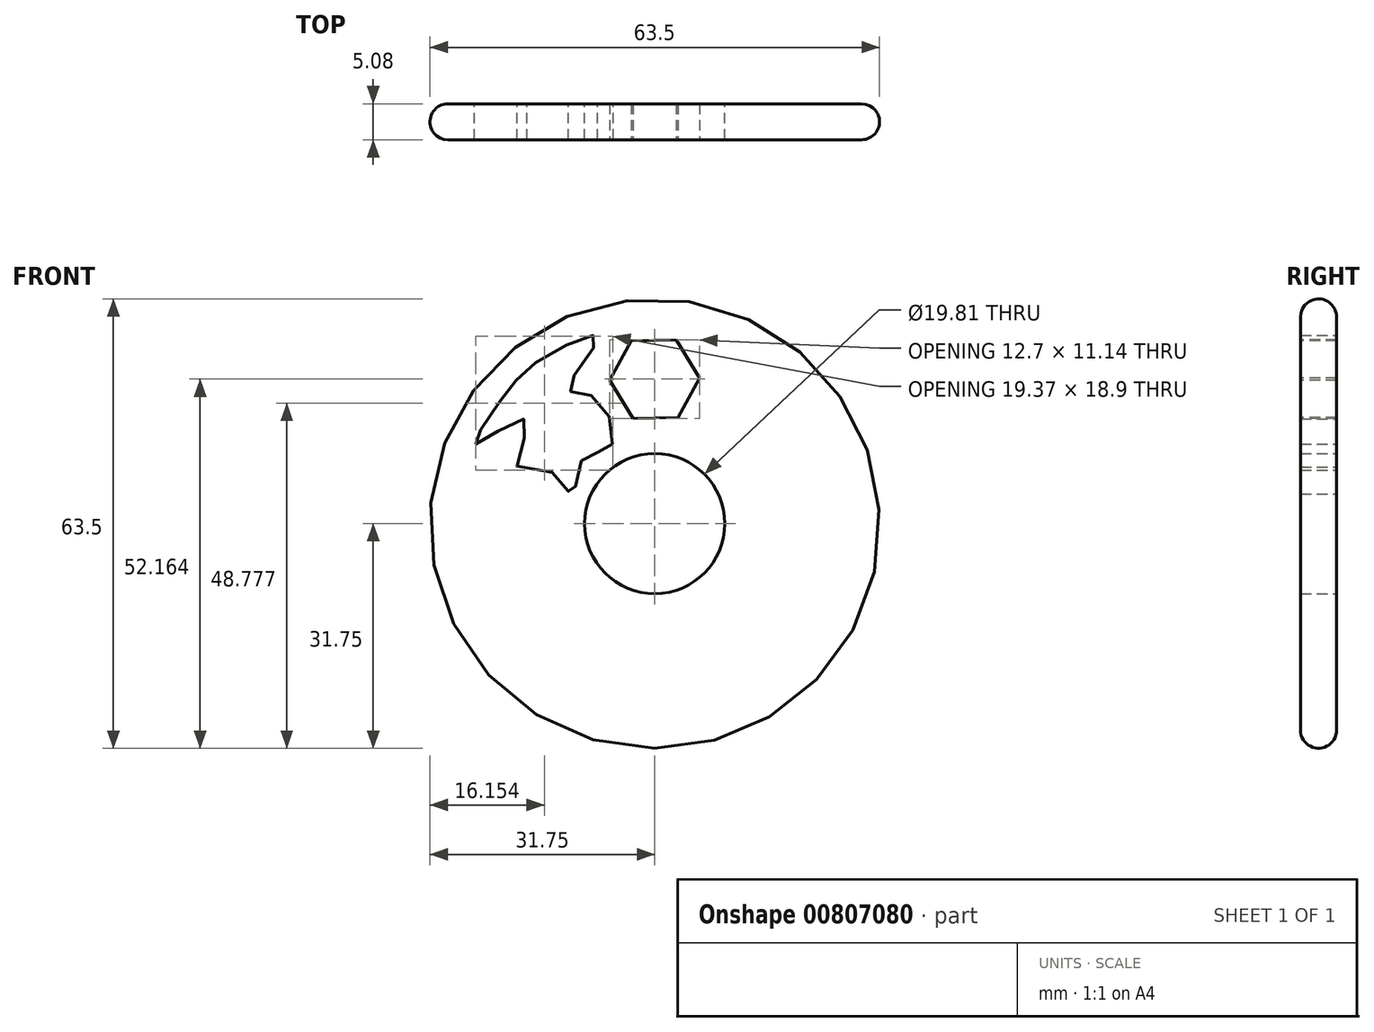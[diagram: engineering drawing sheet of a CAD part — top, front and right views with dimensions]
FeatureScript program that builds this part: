
annotation { "Feature Type Name" : "Feature", "Feature Type Description" : "" }
export const myFeature = defineFeature(function(context is Context, id is Id, definition is map)
    precondition{}
    {
        {
            var Q0;
            Q0=qCreatedBy(makeId("Front.planeOp"),FACE);
            var sketch = newSketch(context, id + "F0", { "sketchPlane" : qUnion([Q0])});
            skCircle(sketch, "E0", {"center": v(0, 0) * mm, "radius": 31.75 * mm});
            skCircle(sketch, "E1", {"center": v(0, 0) * mm, "radius": 9.9 * mm});
            skSolve(sketch);
        }
        {
            var Q0;
            Q0=makeQuery(id+"F0.imprint","IMPRINT",FACE,{"disambiguationData":[TD([[makeQuery(id+"F0.imprint","IMPRINT",EDGE,{"derivedFrom":sQuery(id+"F0.wireOp",EDGE,"E0")}),1.0]])]});
            extrude(context, id + "F1", {"entities" : qUnion([Q0]), "depth" : 5.08 * mm, "offsetDistance" : 25.4 * mm});
        }
        {
            var Q0;
            Q0=makeQuery(id+"F1.opExtrude","CAP_FACE",FACE,{"disambiguationData":[OSD([sQuery(id+"F0.wireOp",EDGE,"E0"),sQuery(id+"F0.wireOp",EDGE,"E1")])],"isStart":false});
            var sketch = newSketch(context, id + "F2", { "sketchPlane" : qUnion([Q0])});
            skCircle(sketch, "E2.cCircle", {"center": v(0, 20.41) * mm, "radius": 6.35 * mm, "construction": true});
            skLineSegment(sketch, "E2.0", {"start": v(6.35, 20.55) * mm, "end": v(3.3, 14.98) * mm});
            skLineSegment(sketch, "E2.1", {"start": v(3.3, 14.98) * mm, "end": v(-3.05, 14.85) * mm});
            skLineSegment(sketch, "E2.2", {"start": v(-3.05, 14.85) * mm, "end": v(-6.35, 20.27) * mm});
            skLineSegment(sketch, "E2.3", {"start": v(-6.35, 20.27) * mm, "end": v(-3.3, 25.84) * mm});
            skLineSegment(sketch, "E2.4", {"start": v(-3.3, 25.84) * mm, "end": v(3.05, 25.98) * mm});
            skLineSegment(sketch, "E2.5", {"start": v(3.05, 25.98) * mm, "end": v(6.35, 20.55) * mm});
            skSolve(sketch);
        }
        {
            var Q0;
            Q0=makeQuery(id+"F2.imprint","IMPRINT",FACE,{"disambiguationData":[TD([[makeQuery(id+"F2.imprint","IMPRINT",EDGE,{"derivedFrom":sQuery(id+"F2.wireOp",EDGE,"E2.0")}),-1.0]])]});
            extrude(context, id + "F3", {"entities" : qUnion([Q0]), "operationType" : NewBodyOperationType.REMOVE, "oppositeDirection" : true, "depth" : 25.4 * mm, "offsetDistance" : 25.4 * mm});
        }
        {
            var Q0;
            Q0=makeQuery(id+"F1.opExtrude","CAP_FACE",FACE,{"disambiguationData":[OSD([sQuery(id+"F0.wireOp",EDGE,"E0"),sQuery(id+"F0.wireOp",EDGE,"E1")])],"isStart":false});
            var sketch = newSketch(context, id + "F4", { "sketchPlane" : qUnion([Q0])});
            skFitSpline(sketch, "E3", {"points": [v(-25.28, 11.23) * mm, v(-21.91, 17.19) * mm, v(-16.06, 23.25) * mm, v(-8.07, 26.26) * mm, v(-12.22, 19.1) * mm, v(-8.33, 17.8) * mm, v(-6.35, 10.6) * mm, v(-10, 9.46) * mm, v(-11.6, 4.18) * mm, v(-15.54, 7.86) * mm, v(-19.43, 7.8) * mm, v(-18.28, 14.7) * mm, v(-25.28, 11.23) * mm]});
            skSolve(sketch);
        }
        {
            var Q0;
            Q0=makeQuery(id+"F4.imprint","IMPRINT",FACE,{"disambiguationData":[TD([[makeQuery(id+"F4.imprint","IMPRINT",EDGE,{"derivedFrom":sQuery(id+"F4.wireOp",EDGE,"E3")}),-1.0]])]});
            extrude(context, id + "F5", {"entities" : qUnion([Q0]), "operationType" : NewBodyOperationType.REMOVE, "oppositeDirection" : true, "depth" : 25.4 * mm, "offsetDistance" : 25.4 * mm});
        }
        {
            var Q0;
            Q0=makeQuery(id+"F1.opExtrude","CAP_EDGE",EDGE,{"disambiguationData":[OSD([sQuery(id+"F0.wireOp",EDGE,"E0")])],"isStart":true});
            var Q1;
            Q1=makeQuery(id+"F1.opExtrude","CAP_EDGE",EDGE,{"disambiguationData":[OSD([sQuery(id+"F0.wireOp",EDGE,"E0")])],"isStart":false});
            fillet(context, id + "F6", {"entities" : qUnion([Q0, Q1]), "radius" : 2.54 * mm, "tangentPropagation" : true, "allowEdgeOverflow" : false});
        }
    });
